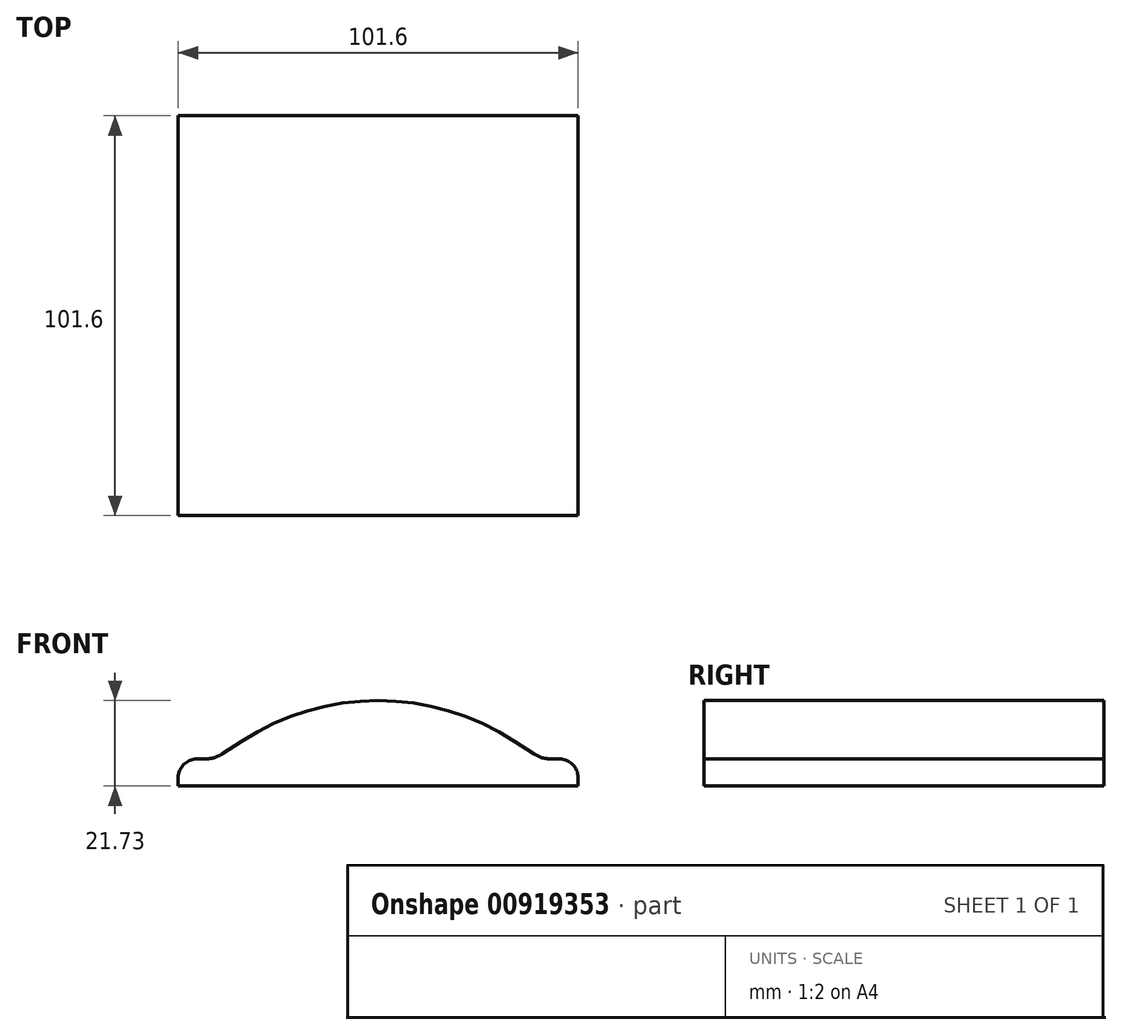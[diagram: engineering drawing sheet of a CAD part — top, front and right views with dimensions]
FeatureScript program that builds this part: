
annotation { "Feature Type Name" : "Feature", "Feature Type Description" : "" }
export const myFeature = defineFeature(function(context is Context, id is Id, definition is map)
    precondition{}
    {
        {
            var Q0;
            Q0=qCreatedBy(makeId("Front.planeOp"),FACE);
            var sketch = newSketch(context, id + "F0", { "sketchPlane" : qUnion([Q0])});
            skLineSegment(sketch, "E0.bottom", {"start": v(-50.55, 0) * mm, "end": v(51.05, 0) * mm});
            skLineSegment(sketch, "E0.right", {"start": v(51.05, 0) * mm, "end": v(51.05, 2.14) * mm});
            skPoint(sketch, "E1.visualSharp", {"position": v(51.05, 6.9) * mm});
            skArc(sketch, "E1.filletArc", {"start": v(51.05, 2.14) * mm, "mid": v(49.65, 5.5) * mm, "end": v(46.28, 6.9) * mm});
            skLineSegment(sketch, "E2.trimOffspring", {"start": v(44.18, 6.9) * mm, "end": v(46.28, 6.9) * mm});
            skLineSegment(sketch, "E3", {"start": v(34.92, 11.4) * mm, "end": v(39.84, 8.2) * mm});
            skPoint(sketch, "E4.visualSharp", {"position": v(41.81, 6.9) * mm});
            skArc(sketch, "E4.filletArc", {"start": v(39.84, 8.2) * mm, "mid": v(41.91, 7.23) * mm, "end": v(44.18, 6.9) * mm});
            skLineSegment(sketch, "E5.MirrorCS", {"start": v(-50.55, 0) * mm, "end": v(-50.55, 2.14) * mm});
            skLineSegment(sketch, "E6.MirrorCS", {"start": v(-43.69, 6.9) * mm, "end": v(-45.8, 6.9) * mm});
            skArc(sketch, "E7.MirrorCS", {"start": v(-39.35, 8.2) * mm, "mid": v(-41.42, 7.23) * mm, "end": v(-43.69, 6.9) * mm});
            skPoint(sketch, "E8.MirrorP", {"position": v(-41.32, 6.9) * mm});
            skArc(sketch, "E9.MirrorCS", {"start": v(-50.55, 2.14) * mm, "mid": v(-49.16, 5.5) * mm, "end": v(-45.8, 6.9) * mm});
            skLineSegment(sketch, "E10.MirrorCS", {"start": v(-34.43, 11.4) * mm, "end": v(-39.35, 8.2) * mm});
            skPoint(sketch, "E11.MirrorP", {"position": v(-50.55, 6.9) * mm});
            skArc(sketch, "E12", {"start": v(34.92, 11.4) * mm, "mid": v(0.25, 21.73) * mm, "end": v(-34.43, 11.4) * mm});
            skPoint(sketch, "E13", {"position": v(0, 0) * mm});
            skSolve(sketch);
        }
        {
            var Q0;
            Q0=makeQuery(id+"F0.imprint","IMPRINT",FACE,{"disambiguationData":[TD([[makeQuery(id+"F0.imprint","IMPRINT",EDGE,{"derivedFrom":sQuery(id+"F0.wireOp",EDGE,"E0.bottom")}),1.0]])]});
            extrude(context, id + "F1", {"entities" : qUnion([Q0]), "depth" : 50.8 * mm, "offsetDistance" : 25.4 * mm, "hasSecondDirection" : true, "secondDirectionOppositeDirection" : true, "secondDirectionDepth" : 50.8 * mm});
        }
    });
